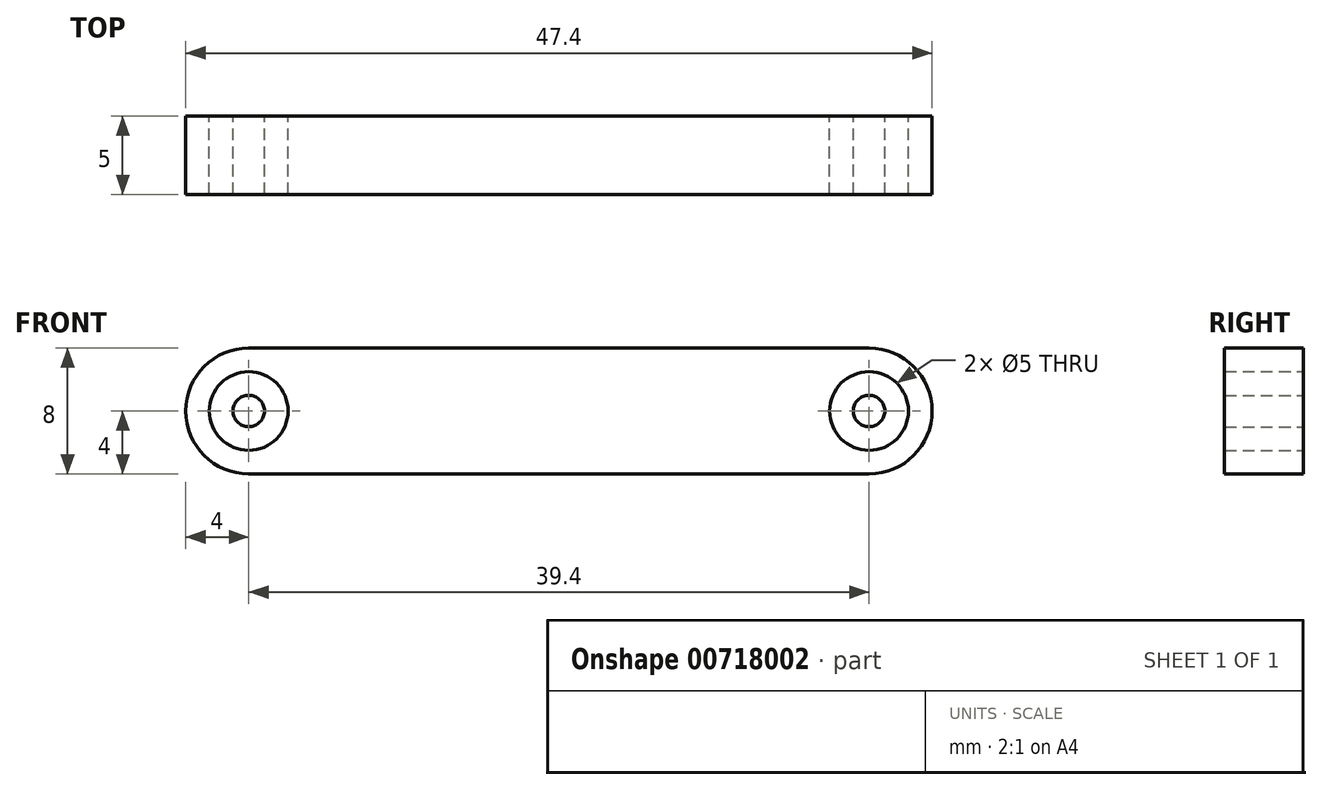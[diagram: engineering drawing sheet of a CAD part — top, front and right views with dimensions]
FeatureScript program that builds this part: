
annotation { "Feature Type Name" : "Feature", "Feature Type Description" : "" }
export const myFeature = defineFeature(function(context is Context, id is Id, definition is map)
    precondition{}
    {
        {
            var Q0;
            Q0=qCreatedBy(makeId("Front.planeOp"),FACE);
            var sketch = newSketch(context, id + "F0", { "sketchPlane" : qUnion([Q0])});
            skCircle(sketch, "E0", {"center": v(0, 0) * mm, "radius": 4 * mm});
            skCircle(sketch, "E1", {"center": v(39.4, 0) * mm, "radius": 4 * mm});
            skLineSegment(sketch, "E2", {"start": v(39.4, 4) * mm, "end": v(0, 4) * mm});
            skLineSegment(sketch, "E3", {"start": v(0, -4) * mm, "end": v(39.4, -4) * mm});
            skCircle(sketch, "E4", {"center": v(0, 0) * mm, "radius": 2.5 * mm});
            skCircle(sketch, "E5", {"center": v(39.4, 0) * mm, "radius": 2.5 * mm});
            skCircle(sketch, "E6", {"center": v(39.4, 0) * mm, "radius": 1 * mm});
            skCircle(sketch, "E7", {"center": v(0, 0) * mm, "radius": 1 * mm});
            skSolve(sketch);
        }
        {
            var Q0;
            Q0 = qSketchRegion(id + "F0", true);
            var Q1;
            Q1=makeQuery(id+"F0.imprint","IMPRINT",FACE,{"disambiguationData":[TD([[makeQuery(id+"F0.imprint","IMPRINT",EDGE,{"derivedFrom":sQuery(id+"F0.wireOp",EDGE,"E7")}),1.0]])]});
            var Q2;
            Q2=makeQuery(id+"F0.imprint","IMPRINT",FACE,{"disambiguationData":[TD([[makeQuery(id+"F0.imprint","IMPRINT",EDGE,{"derivedFrom":sQuery(id+"F0.wireOp",EDGE,"E6")}),1.0]])]});
            extrude(context, id + "F1", {"entities" : qUnion([Q0, Q1, Q2]), "depth" : 5 * mm, "offsetDistance" : 25 * mm});
        }
    });
